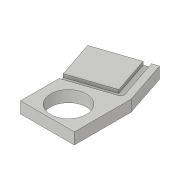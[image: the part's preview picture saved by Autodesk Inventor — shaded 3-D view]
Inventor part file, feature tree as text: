
AUTODESK INVENTOR PART (.ipt)
format: ipt  version: 2018.3 (Build 223284000, 284)  size: 115,200 bytes
history: native  units: in
note: dims shown in document units (in); Inventor stores cm internally (conversion verified against a paired STEP export)
features: extrude x2, sketch x2, fillet x1
ambient origin geometry x8: Origin, YZ Plane, XZ Plane, XY Plane, X Axis, Y Axis, Z Axis, Center Point
bodies: Solid1 (feature_tree)
feature tree (5):
  extrude  "Extrusion1"  Depth=0.22in
  extrude  "Extrusion2"  Depth=0.126in
  fillet  "Fillet1"  Radius=0.0625in
  sketch  "Sketch1"  dims[d0=0.75in d1=0.875in d2=1.1003in d3=1.0432in d4=0.6925in d5=0.22in d6=0.0in d10=0.125in]
  sketch  "Sketch2"  dims[d11=0.126in d12=0.126in d13=0.0625in d14=0.0in d15=0.0in d16=0.0625in d17=0.5216in d18=0.0625in d19=0.5216in d20=0.4088in]
